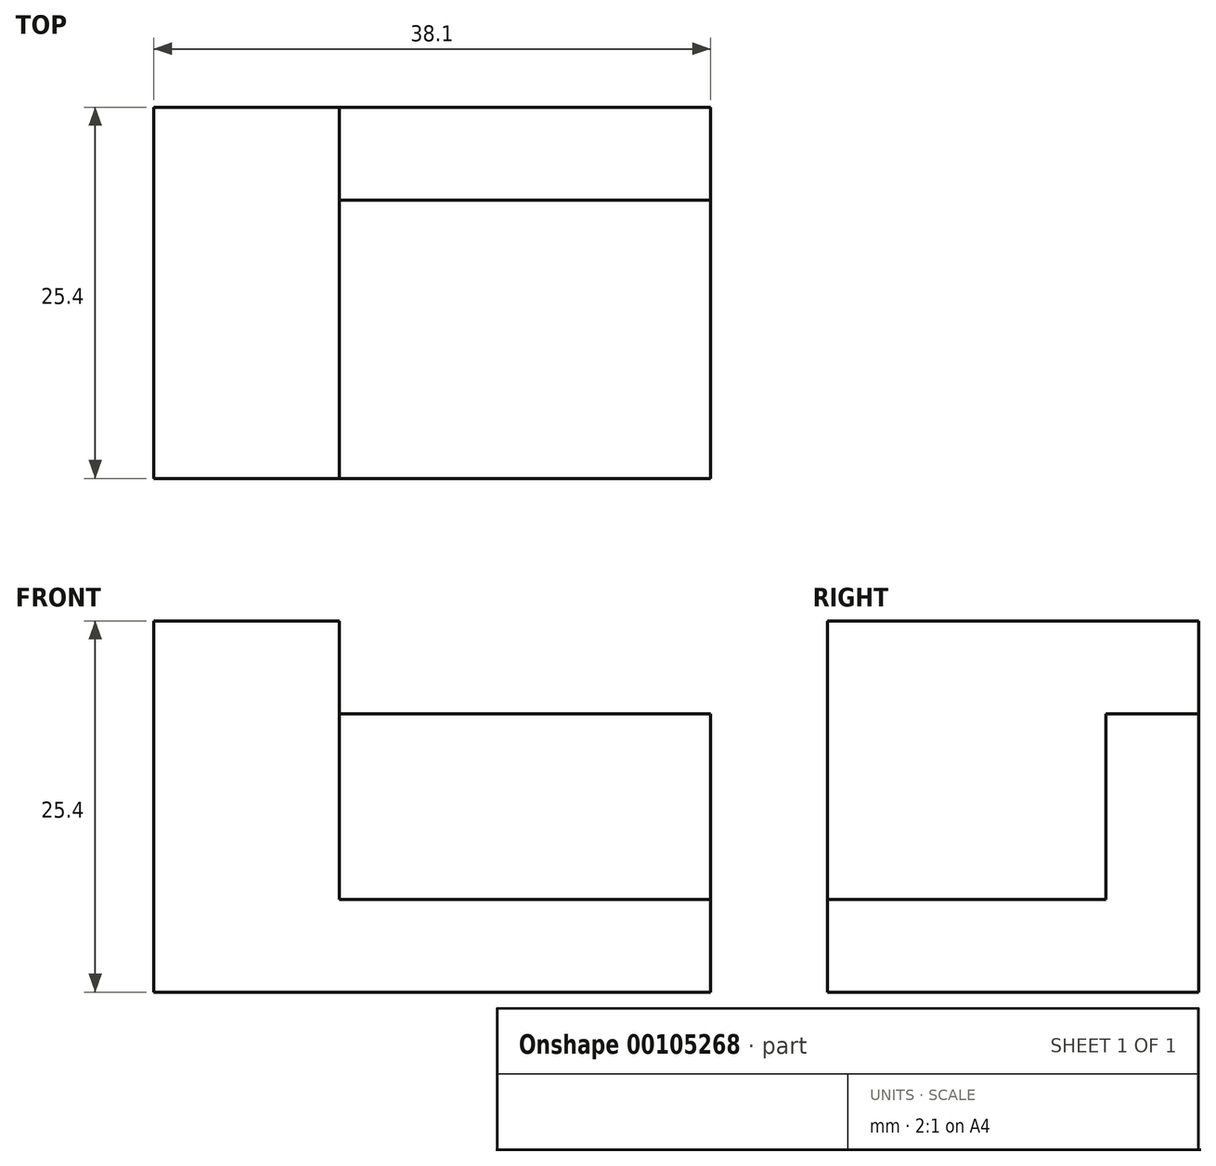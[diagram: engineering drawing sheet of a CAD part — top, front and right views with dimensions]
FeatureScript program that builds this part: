
annotation { "Feature Type Name" : "Feature", "Feature Type Description" : "" }
export const myFeature = defineFeature(function(context is Context, id is Id, definition is map)
    precondition{}
    {
        {
            var Q0;
            Q0=qCreatedBy(makeId("Right.planeOp"),FACE);
            var sketch = newSketch(context, id + "F0", { "sketchPlane" : qUnion([Q0])});
            skLineSegment(sketch, "E0", {"start": v(0, 0) * mm, "end": v(25.4, 0) * mm});
            skLineSegment(sketch, "E1", {"start": v(25.4, 0) * mm, "end": v(25.4, 25.4) * mm});
            skLineSegment(sketch, "E2", {"start": v(25.4, 25.4) * mm, "end": v(0, 25.4) * mm});
            skLineSegment(sketch, "E3", {"start": v(0, 25.4) * mm, "end": v(0, 0) * mm});
            skLineSegment(sketch, "E4", {"start": v(0, 0) * mm, "end": v(0, 6.35) * mm});
            skLineSegment(sketch, "E5", {"start": v(0, 6.35) * mm, "end": v(19.05, 6.35) * mm});
            skLineSegment(sketch, "E6", {"start": v(19.05, 6.35) * mm, "end": v(19.05, 19.05) * mm});
            skLineSegment(sketch, "E7", {"start": v(19.05, 19.05) * mm, "end": v(25.4, 19.05) * mm});
            skLineSegment(sketch, "E8", {"start": v(25.4, 19.05) * mm, "end": v(25.4, 0) * mm});
            skSolve(sketch);
        }
        {
            var Q0;
            Q0=makeQuery(id+"F0.imprint","IMPRINT",FACE,{"disambiguationData":[TD([[makeQuery(id+"F0.imprint","IMPRINT",EDGE,{"derivedFrom":sQuery(id+"F0.wireOp",EDGE,"E1")}),1.0]])]});
            extrude(context, id + "F1", {"entities" : qUnion([Q0]), "depth" : 12.7 * mm});
        }
        {
            var Q0;
            Q0=makeQuery(id+"F0.imprint","IMPRINT",FACE,{"disambiguationData":[TD([[makeQuery(id+"F0.imprint","IMPRINT",EDGE,{"derivedFrom":sQuery(id+"F0.wireOp",EDGE,"E0")}),1.0]])]});
            extrude(context, id + "F2", {"entities" : qUnion([Q0]), "operationType" : NewBodyOperationType.ADD, "depth" : 38.1 * mm});
        }
    });
